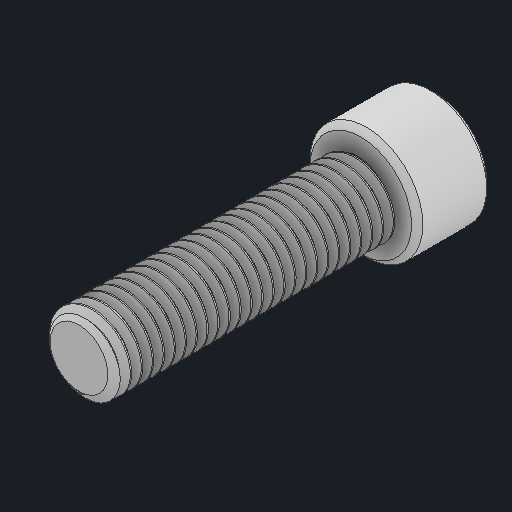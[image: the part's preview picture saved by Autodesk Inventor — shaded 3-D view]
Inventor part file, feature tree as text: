
AUTODESK INVENTOR PART (.ipt)
format: ipt  version: 2025 (Build 290162000, 162)  size: 920,064 bytes
history: native  units: in
note: dims shown in document units (in); Inventor stores cm internally (conversion verified against a paired STEP export)
features: chamfer x1
ambient origin geometry x8: Origin, YZ Plane, XZ Plane, XY Plane, X Axis, Y Axis, Z Axis, Center Point
bodies: Solid1 (feature_tree)
feature tree (1):
  chamfer  "Chamfer1"  [1 undecoded]
note: 1 required parameter value undecoded (feature->parameter linkage not recoverable at this tier; creation-order binding heuristic only, values carry confidence <= 0.55)
